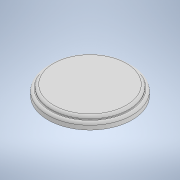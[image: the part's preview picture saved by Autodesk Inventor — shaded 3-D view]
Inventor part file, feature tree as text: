
AUTODESK INVENTOR PART (.ipt)
format: ipt  version: 2022 (Build 260153000, 153)  size: 130,560 bytes
history: native  units: mm
features: revolve x1, fillet x1, sketch x1
ambient origin geometry x8: Origin, YZ Plane, XZ Plane, XY Plane, X Axis, Y Axis, Z Axis, Center Point
bodies: Solid1 (feature_tree)
feature tree (3):
  revolve  "Revolution1"  [1 undecoded]
  fillet  "Fillet1"  Radius=1.0mm
  sketch  "Sketch1"  dims[d0=12.7mm d1=2.0mm d2=1.0mm d3=1.0mm d4=90.0deg d5=0.75mm]
note: 1 required parameter value undecoded (feature->parameter linkage not recoverable at this tier; creation-order binding heuristic only, values carry confidence <= 0.55)
